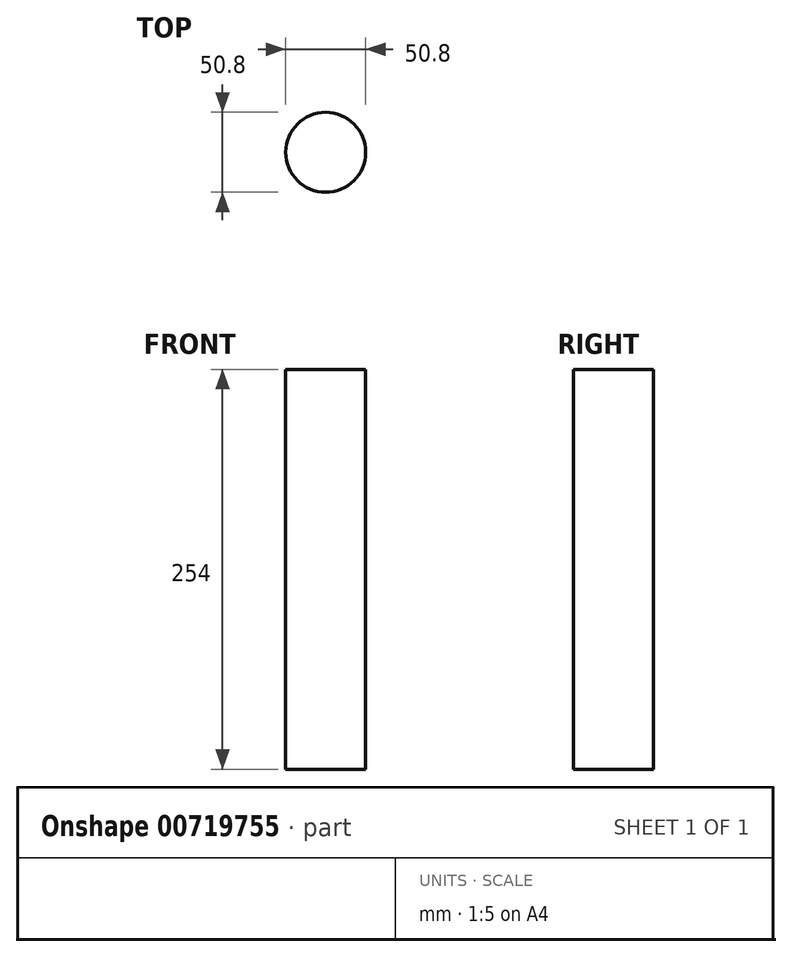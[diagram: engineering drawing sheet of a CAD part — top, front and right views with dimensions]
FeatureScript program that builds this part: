
annotation { "Feature Type Name" : "Feature", "Feature Type Description" : "" }
export const myFeature = defineFeature(function(context is Context, id is Id, definition is map)
    precondition{}
    {
        {
            var Q0;
            Q0=qCreatedBy(makeId("Top.planeOp"),FACE);
            var sketch = newSketch(context, id + "F0", { "sketchPlane" : qUnion([Q0])});
            skCircle(sketch, "E0", {"center": v(0, 0) * mm, "radius": 25.4 * mm});
            skSolve(sketch);
        }
        {
            var Q0;
            Q0 = qSketchRegion(id + "F0", true);
            extrude(context, id + "F1", {"entities" : qUnion([Q0]), "depth" : 254 * mm, "offsetDistance" : 25.4 * mm});
        }
    });
